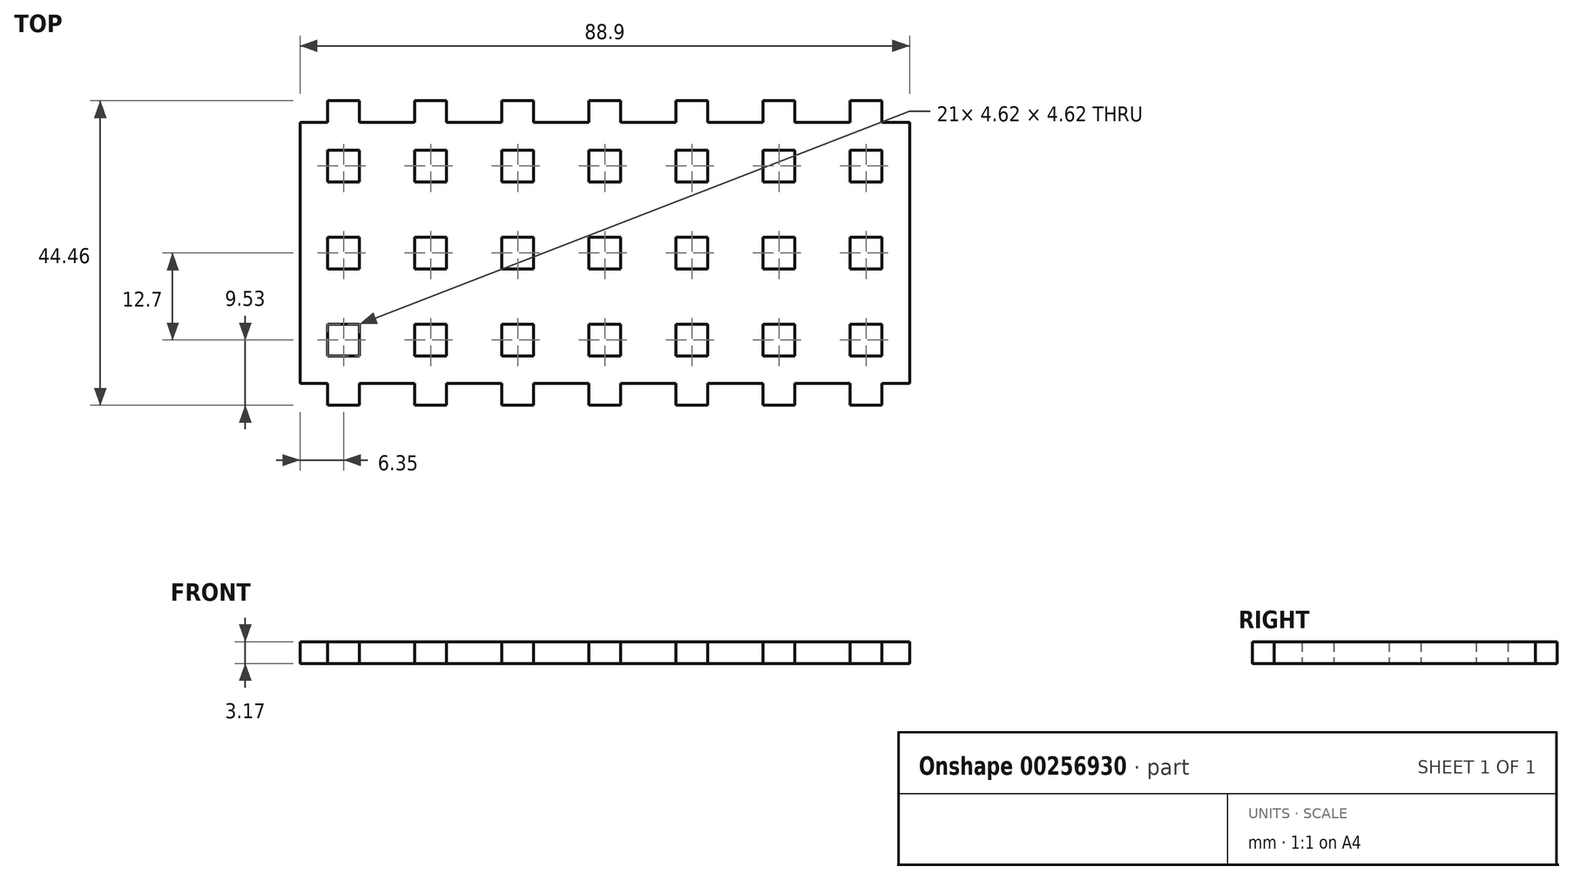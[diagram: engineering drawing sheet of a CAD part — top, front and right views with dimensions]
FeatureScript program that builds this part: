
annotation { "Feature Type Name" : "Feature", "Feature Type Description" : "" }
export const myFeature = defineFeature(function(context is Context, id is Id, definition is map)
    precondition{}
    {
        {
            var Q0;
            Q0=qCreatedBy(makeId("Top.planeOp"),FACE);
            var sketch = newSketch(context, id + "F0", { "sketchPlane" : qUnion([Q0])});
            skLineSegment(sketch, "E0.bottom", {"start": v(44.45, 19.05) * mm, "end": v(-44.45, 19.05) * mm});
            skLineSegment(sketch, "E0.top", {"start": v(44.45, -19.05) * mm, "end": v(-44.45, -19.05) * mm});
            skLineSegment(sketch, "E0.left", {"start": v(44.45, 19.05) * mm, "end": v(44.45, -19.05) * mm});
            skLineSegment(sketch, "E0.right", {"start": v(-44.45, 19.05) * mm, "end": v(-44.45, -19.05) * mm});
            skLineSegment(sketch, "E1", {"start": v(-44.45, -19.05) * mm, "end": v(-38.1, -19.05) * mm});
            skLineSegment(sketch, "E2.top", {"start": v(-35.79, -22.22) * mm, "end": v(-40.41, -22.22) * mm});
            skLineSegment(sketch, "E2.left", {"start": v(-35.79, -19.05) * mm, "end": v(-35.79, -22.22) * mm});
            skLineSegment(sketch, "E2.right", {"start": v(-40.41, -19.05) * mm, "end": v(-40.41, -22.22) * mm});
            skPoint(sketch, "E2.middle", {"position": v(-38.1, -19.05) * mm});
            skPoint(sketch, "E2.bottom.start.orphan", {"position": v(-35.79, -15.87) * mm});
            skPoint(sketch, "E3.orphan", {"position": v(-40.41, -15.87) * mm});
            skLineSegment(sketch, "E4.1.0.0", {"start": v(-23.09, -19.05) * mm, "end": v(-23.09, -22.22) * mm});
            skLineSegment(sketch, "E4.1.0.1", {"start": v(-27.71, -19.05) * mm, "end": v(-27.71, -22.22) * mm});
            skLineSegment(sketch, "E4.1.0.2", {"start": v(-23.09, -22.22) * mm, "end": v(-27.71, -22.22) * mm});
            skLineSegment(sketch, "E4.2.0.0", {"start": v(-10.39, -19.05) * mm, "end": v(-10.39, -22.22) * mm});
            skLineSegment(sketch, "E4.2.0.1", {"start": v(-15.01, -19.05) * mm, "end": v(-15.01, -22.22) * mm});
            skLineSegment(sketch, "E4.2.0.2", {"start": v(-10.39, -22.22) * mm, "end": v(-15.01, -22.22) * mm});
            skLineSegment(sketch, "E4.3.0.0", {"start": v(2.31, -19.05) * mm, "end": v(2.31, -22.22) * mm});
            skLineSegment(sketch, "E4.3.0.1", {"start": v(-2.31, -19.05) * mm, "end": v(-2.31, -22.22) * mm});
            skLineSegment(sketch, "E4.3.0.2", {"start": v(2.31, -22.22) * mm, "end": v(-2.31, -22.22) * mm});
            skLineSegment(sketch, "E4.4.0.0", {"start": v(15.01, -19.05) * mm, "end": v(15.01, -22.22) * mm});
            skLineSegment(sketch, "E4.4.0.1", {"start": v(10.39, -19.05) * mm, "end": v(10.39, -22.22) * mm});
            skLineSegment(sketch, "E4.4.0.2", {"start": v(15.01, -22.22) * mm, "end": v(10.39, -22.22) * mm});
            skLineSegment(sketch, "E4.5.0.0", {"start": v(27.71, -19.05) * mm, "end": v(27.71, -22.22) * mm});
            skLineSegment(sketch, "E4.5.0.1", {"start": v(23.09, -19.05) * mm, "end": v(23.09, -22.22) * mm});
            skLineSegment(sketch, "E4.5.0.2", {"start": v(27.71, -22.22) * mm, "end": v(23.09, -22.22) * mm});
            skLineSegment(sketch, "E4.6.0.0", {"start": v(40.41, -19.05) * mm, "end": v(40.41, -22.22) * mm});
            skLineSegment(sketch, "E4.6.0.1", {"start": v(35.79, -19.05) * mm, "end": v(35.79, -22.22) * mm});
            skLineSegment(sketch, "E4.6.0.2", {"start": v(40.41, -22.22) * mm, "end": v(35.79, -22.22) * mm});
            skLineSegment(sketch, "E4.direction1", {"start": v(-35.79, -22.22) * mm, "end": v(-23.09, -22.22) * mm, "construction": true});
            skLineSegment(sketch, "E5.MirrorCS", {"start": v(-2.31, 19.05) * mm, "end": v(-2.31, 22.22) * mm});
            skLineSegment(sketch, "E6.MirrorCS", {"start": v(35.79, 19.05) * mm, "end": v(35.79, 22.22) * mm});
            skLineSegment(sketch, "E7.MirrorCS", {"start": v(15.01, 19.05) * mm, "end": v(15.01, 22.22) * mm});
            skLineSegment(sketch, "E8.MirrorCS", {"start": v(-10.39, 19.05) * mm, "end": v(-10.39, 22.22) * mm});
            skLineSegment(sketch, "E9.MirrorCS", {"start": v(-15.01, 19.05) * mm, "end": v(-15.01, 22.22) * mm});
            skLineSegment(sketch, "E10.MirrorCS", {"start": v(40.41, 19.05) * mm, "end": v(40.41, 22.22) * mm});
            skLineSegment(sketch, "E11.MirrorCS", {"start": v(27.71, 19.05) * mm, "end": v(27.71, 22.22) * mm});
            skLineSegment(sketch, "E12.MirrorCS", {"start": v(-44.45, 19.05) * mm, "end": v(-38.1, 19.05) * mm});
            skLineSegment(sketch, "E13.MirrorCS", {"start": v(-35.79, 19.05) * mm, "end": v(-35.79, 22.22) * mm});
            skLineSegment(sketch, "E14.MirrorCS", {"start": v(-40.41, 19.05) * mm, "end": v(-40.41, 22.22) * mm});
            skLineSegment(sketch, "E15.MirrorCS", {"start": v(-23.09, 19.05) * mm, "end": v(-23.09, 22.22) * mm});
            skLineSegment(sketch, "E16.MirrorCS", {"start": v(2.31, 19.05) * mm, "end": v(2.31, 22.22) * mm});
            skLineSegment(sketch, "E17.MirrorCS", {"start": v(23.09, 19.05) * mm, "end": v(23.09, 22.22) * mm});
            skLineSegment(sketch, "E18.MirrorCS", {"start": v(10.39, 19.05) * mm, "end": v(10.39, 22.22) * mm});
            skLineSegment(sketch, "E19.MirrorCS", {"start": v(-23.09, 22.22) * mm, "end": v(-27.71, 22.22) * mm});
            skLineSegment(sketch, "E20.MirrorCS", {"start": v(-27.71, 19.05) * mm, "end": v(-27.71, 22.22) * mm});
            skLineSegment(sketch, "E21.MirrorCS", {"start": v(-10.39, 22.22) * mm, "end": v(-15.01, 22.22) * mm});
            skLineSegment(sketch, "E22.MirrorCS", {"start": v(2.31, 22.22) * mm, "end": v(-2.31, 22.22) * mm});
            skLineSegment(sketch, "E23.MirrorCS", {"start": v(-35.79, 22.22) * mm, "end": v(-40.41, 22.22) * mm});
            skLineSegment(sketch, "E24.MirrorCS", {"start": v(15.01, 22.22) * mm, "end": v(10.39, 22.22) * mm});
            skLineSegment(sketch, "E25.MirrorCS", {"start": v(27.71, 22.22) * mm, "end": v(23.09, 22.22) * mm});
            skLineSegment(sketch, "E26.MirrorCS", {"start": v(-35.79, 22.22) * mm, "end": v(-23.09, 22.22) * mm, "construction": true});
            skLineSegment(sketch, "E27.MirrorCS", {"start": v(40.41, 22.22) * mm, "end": v(35.79, 22.22) * mm});
            skLineSegment(sketch, "E28.left", {"start": v(-44.45, -19.05) * mm, "end": v(-44.45, -12.7) * mm});
            skLineSegment(sketch, "E29.bottom", {"start": v(-35.79, -15.01) * mm, "end": v(-40.41, -15.01) * mm});
            skLineSegment(sketch, "E29.top", {"start": v(-35.79, -10.39) * mm, "end": v(-40.41, -10.39) * mm});
            skLineSegment(sketch, "E29.left", {"start": v(-35.79, -15.01) * mm, "end": v(-35.79, -10.39) * mm});
            skLineSegment(sketch, "E29.right", {"start": v(-40.41, -15.01) * mm, "end": v(-40.41, -10.39) * mm});
            skPoint(sketch, "E29.middle", {"position": v(-38.1, -12.7) * mm});
            skLineSegment(sketch, "E30.1.0.0", {"start": v(-23.09, -10.39) * mm, "end": v(-27.71, -10.39) * mm});
            skLineSegment(sketch, "E30.1.0.1", {"start": v(-27.71, -15.01) * mm, "end": v(-27.71, -10.39) * mm});
            skLineSegment(sketch, "E30.1.0.2", {"start": v(-23.09, -15.01) * mm, "end": v(-27.71, -15.01) * mm});
            skLineSegment(sketch, "E30.1.0.3", {"start": v(-23.09, -15.01) * mm, "end": v(-23.09, -10.39) * mm});
            skLineSegment(sketch, "E30.2.0.0", {"start": v(-10.39, -10.39) * mm, "end": v(-15.01, -10.39) * mm});
            skLineSegment(sketch, "E30.2.0.1", {"start": v(-15.01, -15.01) * mm, "end": v(-15.01, -10.39) * mm});
            skLineSegment(sketch, "E30.2.0.2", {"start": v(-10.39, -15.01) * mm, "end": v(-15.01, -15.01) * mm});
            skLineSegment(sketch, "E30.2.0.3", {"start": v(-10.39, -15.01) * mm, "end": v(-10.39, -10.39) * mm});
            skLineSegment(sketch, "E30.3.0.0", {"start": v(2.31, -10.39) * mm, "end": v(-2.31, -10.39) * mm});
            skLineSegment(sketch, "E30.3.0.1", {"start": v(-2.31, -15.01) * mm, "end": v(-2.31, -10.39) * mm});
            skLineSegment(sketch, "E30.3.0.2", {"start": v(2.31, -15.01) * mm, "end": v(-2.31, -15.01) * mm});
            skLineSegment(sketch, "E30.3.0.3", {"start": v(2.31, -15.01) * mm, "end": v(2.31, -10.39) * mm});
            skLineSegment(sketch, "E30.4.0.0", {"start": v(15.01, -10.39) * mm, "end": v(10.39, -10.39) * mm});
            skLineSegment(sketch, "E30.4.0.1", {"start": v(10.39, -15.01) * mm, "end": v(10.39, -10.39) * mm});
            skLineSegment(sketch, "E30.4.0.2", {"start": v(15.01, -15.01) * mm, "end": v(10.39, -15.01) * mm});
            skLineSegment(sketch, "E30.4.0.3", {"start": v(15.01, -15.01) * mm, "end": v(15.01, -10.39) * mm});
            skLineSegment(sketch, "E30.5.0.0", {"start": v(27.71, -10.39) * mm, "end": v(23.09, -10.39) * mm});
            skLineSegment(sketch, "E30.5.0.1", {"start": v(23.09, -15.01) * mm, "end": v(23.09, -10.39) * mm});
            skLineSegment(sketch, "E30.5.0.2", {"start": v(27.71, -15.01) * mm, "end": v(23.09, -15.01) * mm});
            skLineSegment(sketch, "E30.5.0.3", {"start": v(27.71, -15.01) * mm, "end": v(27.71, -10.39) * mm});
            skLineSegment(sketch, "E30.6.0.0", {"start": v(40.41, -10.39) * mm, "end": v(35.79, -10.39) * mm});
            skLineSegment(sketch, "E30.6.0.1", {"start": v(35.79, -15.01) * mm, "end": v(35.79, -10.39) * mm});
            skLineSegment(sketch, "E30.6.0.2", {"start": v(40.41, -15.01) * mm, "end": v(35.79, -15.01) * mm});
            skLineSegment(sketch, "E30.6.0.3", {"start": v(40.41, -15.01) * mm, "end": v(40.41, -10.39) * mm});
            skLineSegment(sketch, "E30.direction1", {"start": v(-40.41, -10.39) * mm, "end": v(-27.71, -10.39) * mm, "construction": true});
            skPoint(sketch, "E31.0.1.0", {"position": v(-40.41, -3.17) * mm});
            skPoint(sketch, "E31.0.1.1", {"position": v(-38.1, 0) * mm});
            skLineSegment(sketch, "E31.0.1.2", {"start": v(27.71, 2.31) * mm, "end": v(23.09, 2.31) * mm});
            skLineSegment(sketch, "E31.0.1.3", {"start": v(2.31, -2.31) * mm, "end": v(2.31, 2.31) * mm});
            skLineSegment(sketch, "E31.0.1.4", {"start": v(-40.41, -2.31) * mm, "end": v(-40.41, 2.31) * mm});
            skLineSegment(sketch, "E31.0.1.5", {"start": v(-23.09, -2.31) * mm, "end": v(-27.71, -2.31) * mm});
            skLineSegment(sketch, "E31.0.1.6", {"start": v(2.31, -2.31) * mm, "end": v(-2.31, -2.31) * mm});
            skLineSegment(sketch, "E31.0.1.7", {"start": v(-10.39, -2.31) * mm, "end": v(-10.39, 2.31) * mm});
            skLineSegment(sketch, "E31.0.1.8", {"start": v(-23.09, 2.31) * mm, "end": v(-27.71, 2.31) * mm});
            skLineSegment(sketch, "E31.0.1.9", {"start": v(-10.39, -2.31) * mm, "end": v(-15.01, -2.31) * mm});
            skPoint(sketch, "E31.0.1.10", {"position": v(-35.79, -3.17) * mm});
            skLineSegment(sketch, "E31.0.1.11", {"start": v(15.01, 2.31) * mm, "end": v(10.39, 2.31) * mm});
            skLineSegment(sketch, "E31.0.1.12", {"start": v(15.01, -2.31) * mm, "end": v(15.01, 2.31) * mm});
            skLineSegment(sketch, "E31.0.1.13", {"start": v(10.39, -2.31) * mm, "end": v(10.39, 2.31) * mm});
            skLineSegment(sketch, "E31.0.1.14", {"start": v(2.31, 2.31) * mm, "end": v(-2.31, 2.31) * mm});
            skLineSegment(sketch, "E31.0.1.15", {"start": v(-40.41, 2.31) * mm, "end": v(-27.71, 2.31) * mm, "construction": true});
            skLineSegment(sketch, "E31.0.1.16", {"start": v(-35.79, -2.31) * mm, "end": v(-35.79, 2.31) * mm});
            skLineSegment(sketch, "E31.0.1.17", {"start": v(27.71, -2.31) * mm, "end": v(23.09, -2.31) * mm});
            skLineSegment(sketch, "E31.0.1.18", {"start": v(-2.31, -2.31) * mm, "end": v(-2.31, 2.31) * mm});
            skLineSegment(sketch, "E31.0.1.19", {"start": v(40.41, -2.31) * mm, "end": v(40.41, 2.31) * mm});
            skLineSegment(sketch, "E31.0.1.20", {"start": v(15.01, -2.31) * mm, "end": v(10.39, -2.31) * mm});
            skLineSegment(sketch, "E31.0.1.21", {"start": v(-27.71, -2.31) * mm, "end": v(-27.71, 2.31) * mm});
            skLineSegment(sketch, "E31.0.1.22", {"start": v(40.41, 2.31) * mm, "end": v(35.79, 2.31) * mm});
            skLineSegment(sketch, "E31.0.1.23", {"start": v(-10.39, 2.31) * mm, "end": v(-15.01, 2.31) * mm});
            skLineSegment(sketch, "E31.0.1.24", {"start": v(23.09, -2.31) * mm, "end": v(23.09, 2.31) * mm});
            skLineSegment(sketch, "E31.0.1.25", {"start": v(-23.09, -2.31) * mm, "end": v(-23.09, 2.31) * mm});
            skLineSegment(sketch, "E31.0.1.26", {"start": v(27.71, -2.31) * mm, "end": v(27.71, 2.31) * mm});
            skLineSegment(sketch, "E31.0.1.27", {"start": v(35.79, -2.31) * mm, "end": v(35.79, 2.31) * mm});
            skLineSegment(sketch, "E31.0.1.28", {"start": v(-15.01, -2.31) * mm, "end": v(-15.01, 2.31) * mm});
            skLineSegment(sketch, "E31.0.1.29", {"start": v(40.41, -2.31) * mm, "end": v(35.79, -2.31) * mm});
            skLineSegment(sketch, "E31.0.1.30", {"start": v(-35.79, -2.31) * mm, "end": v(-40.41, -2.31) * mm});
            skLineSegment(sketch, "E31.0.1.31", {"start": v(-35.79, 2.31) * mm, "end": v(-40.41, 2.31) * mm});
            skPoint(sketch, "E31.0.2.0", {"position": v(-40.41, 9.53) * mm});
            skPoint(sketch, "E31.0.2.1", {"position": v(-38.1, 12.7) * mm});
            skLineSegment(sketch, "E31.0.2.2", {"start": v(27.71, 15.01) * mm, "end": v(23.09, 15.01) * mm});
            skLineSegment(sketch, "E31.0.2.3", {"start": v(2.31, 10.39) * mm, "end": v(2.31, 15.01) * mm});
            skLineSegment(sketch, "E31.0.2.4", {"start": v(-40.41, 10.39) * mm, "end": v(-40.41, 15.01) * mm});
            skLineSegment(sketch, "E31.0.2.5", {"start": v(-23.09, 10.39) * mm, "end": v(-27.71, 10.39) * mm});
            skLineSegment(sketch, "E31.0.2.6", {"start": v(2.31, 10.39) * mm, "end": v(-2.31, 10.39) * mm});
            skLineSegment(sketch, "E31.0.2.7", {"start": v(-10.39, 10.39) * mm, "end": v(-10.39, 15.01) * mm});
            skLineSegment(sketch, "E31.0.2.8", {"start": v(-23.09, 15.01) * mm, "end": v(-27.71, 15.01) * mm});
            skLineSegment(sketch, "E31.0.2.9", {"start": v(-10.39, 10.39) * mm, "end": v(-15.01, 10.39) * mm});
            skPoint(sketch, "E31.0.2.10", {"position": v(-35.79, 9.53) * mm});
            skLineSegment(sketch, "E31.0.2.11", {"start": v(15.01, 15.01) * mm, "end": v(10.39, 15.01) * mm});
            skLineSegment(sketch, "E31.0.2.12", {"start": v(15.01, 10.39) * mm, "end": v(15.01, 15.01) * mm});
            skLineSegment(sketch, "E31.0.2.13", {"start": v(10.39, 10.39) * mm, "end": v(10.39, 15.01) * mm});
            skLineSegment(sketch, "E31.0.2.14", {"start": v(2.31, 15.01) * mm, "end": v(-2.31, 15.01) * mm});
            skLineSegment(sketch, "E31.0.2.15", {"start": v(-40.41, 15.01) * mm, "end": v(-27.71, 15.01) * mm, "construction": true});
            skLineSegment(sketch, "E31.0.2.16", {"start": v(-35.79, 10.39) * mm, "end": v(-35.79, 15.01) * mm});
            skLineSegment(sketch, "E31.0.2.17", {"start": v(27.71, 10.39) * mm, "end": v(23.09, 10.39) * mm});
            skLineSegment(sketch, "E31.0.2.18", {"start": v(-2.31, 10.39) * mm, "end": v(-2.31, 15.01) * mm});
            skLineSegment(sketch, "E31.0.2.19", {"start": v(40.41, 10.39) * mm, "end": v(40.41, 15.01) * mm});
            skLineSegment(sketch, "E31.0.2.20", {"start": v(15.01, 10.39) * mm, "end": v(10.39, 10.39) * mm});
            skLineSegment(sketch, "E31.0.2.21", {"start": v(-27.71, 10.39) * mm, "end": v(-27.71, 15.01) * mm});
            skLineSegment(sketch, "E31.0.2.22", {"start": v(40.41, 15.01) * mm, "end": v(35.79, 15.01) * mm});
            skLineSegment(sketch, "E31.0.2.23", {"start": v(-10.39, 15.01) * mm, "end": v(-15.01, 15.01) * mm});
            skLineSegment(sketch, "E31.0.2.24", {"start": v(23.09, 10.39) * mm, "end": v(23.09, 15.01) * mm});
            skLineSegment(sketch, "E31.0.2.25", {"start": v(-23.09, 10.39) * mm, "end": v(-23.09, 15.01) * mm});
            skLineSegment(sketch, "E31.0.2.26", {"start": v(27.71, 10.39) * mm, "end": v(27.71, 15.01) * mm});
            skLineSegment(sketch, "E31.0.2.27", {"start": v(35.79, 10.39) * mm, "end": v(35.79, 15.01) * mm});
            skLineSegment(sketch, "E31.0.2.28", {"start": v(-15.01, 10.39) * mm, "end": v(-15.01, 15.01) * mm});
            skLineSegment(sketch, "E31.0.2.29", {"start": v(40.41, 10.39) * mm, "end": v(35.79, 10.39) * mm});
            skLineSegment(sketch, "E31.0.2.30", {"start": v(-35.79, 10.39) * mm, "end": v(-40.41, 10.39) * mm});
            skLineSegment(sketch, "E31.0.2.31", {"start": v(-35.79, 15.01) * mm, "end": v(-40.41, 15.01) * mm});
            skLineSegment(sketch, "E31.direction1", {"start": v(-40.41, -15.87) * mm, "end": v(-15.01, -15.87) * mm, "construction": true});
            skLineSegment(sketch, "E31.direction2", {"start": v(-40.41, -15.87) * mm, "end": v(-40.41, -3.17) * mm, "construction": true});
            skSolve(sketch);
        }
        {
            var Q0;
            Q0 = qSketchRegion(id + "F0", true);
            extrude(context, id + "F1", {"entities" : qUnion([Q0]), "depth" : 3.17 * mm});
        }
    });
